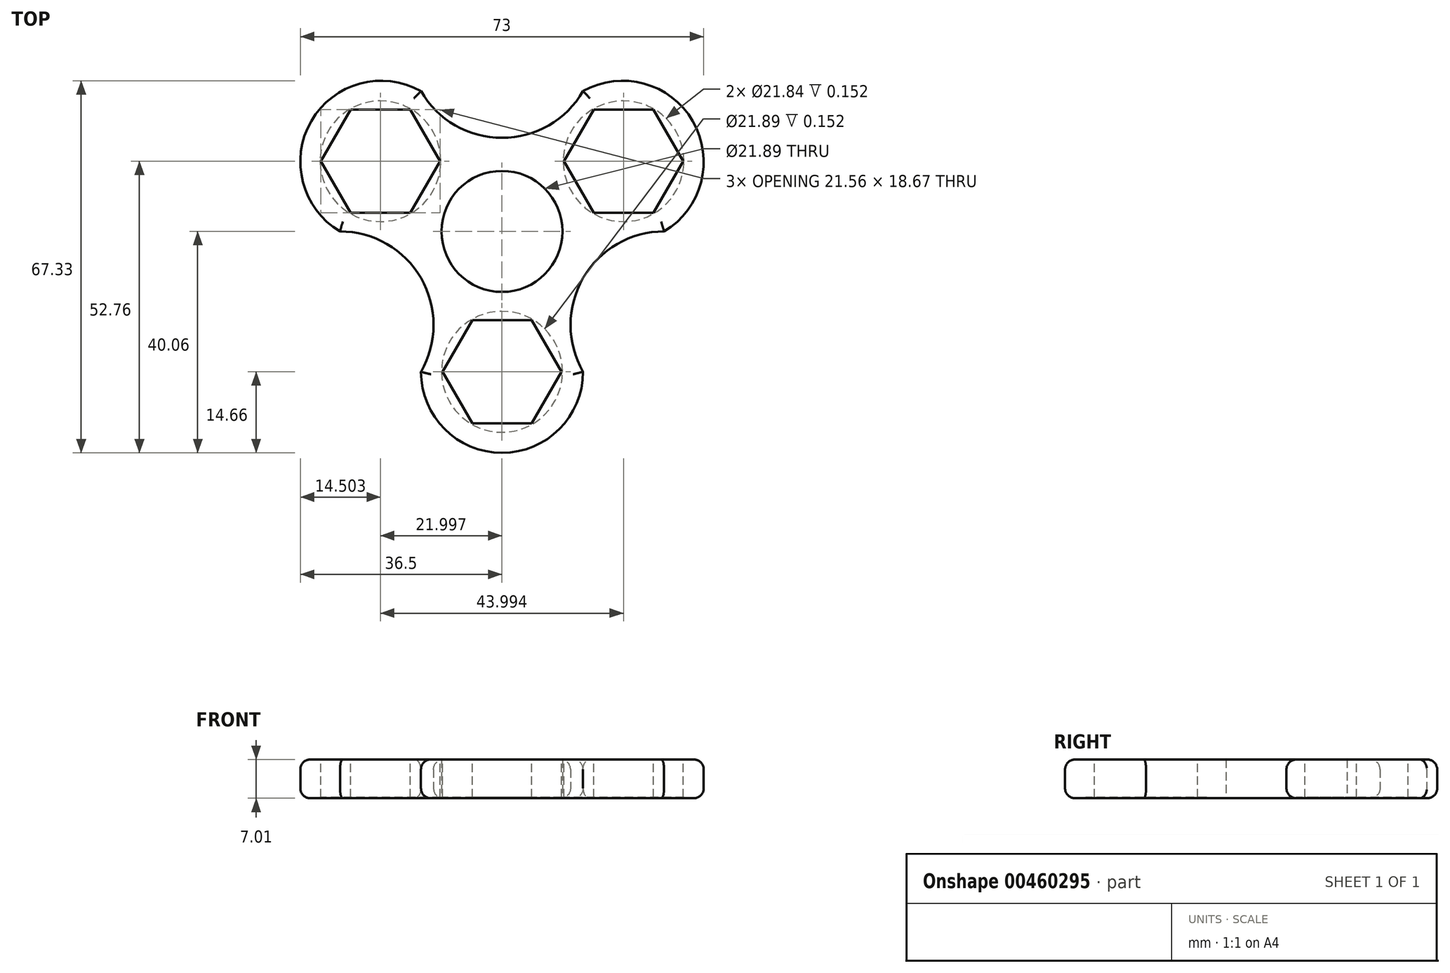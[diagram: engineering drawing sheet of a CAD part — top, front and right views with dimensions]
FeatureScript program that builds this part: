
annotation { "Feature Type Name" : "Feature", "Feature Type Description" : "" }
export const myFeature = defineFeature(function(context is Context, id is Id, definition is map)
    precondition{}
    {
        {
            var Q0;
            Q0=qCreatedBy(makeId("Top.planeOp"),FACE);
            var sketch = newSketch(context, id + "F0", { "sketchPlane" : qUnion([Q0])});
            skCircle(sketch, "E0.cCircle", {"center": v(0, 0) * mm, "radius": 12.7 * mm, "construction": true});
            skLineSegment(sketch, "E0.0", {"start": v(7.33, -12.7) * mm, "end": v(-7.33, -12.7) * mm});
            skLineSegment(sketch, "E0.1", {"start": v(-7.33, -12.7) * mm, "end": v(-14.66, 0) * mm});
            skLineSegment(sketch, "E0.2", {"start": v(-14.66, 0) * mm, "end": v(-7.33, 12.7) * mm});
            skLineSegment(sketch, "E0.4", {"start": v(7.33, 12.7) * mm, "end": v(14.66, 0) * mm});
            skLineSegment(sketch, "E0.5", {"start": v(14.66, 0) * mm, "end": v(7.33, -12.7) * mm});
            skCircle(sketch, "E1", {"center": v(0, 0) * mm, "radius": 10.95 * mm});
            skLineSegment(sketch, "E2.bottom", {"start": v(6.06, -12.7) * mm, "end": v(-4.9, -12.7) * mm});
            skLineSegment(sketch, "E3.MirrorCS", {"start": v(4.8, -76.2) * mm, "end": v(-4.8, -76.2) * mm});
            skLineSegment(sketch, "E4.MirrorCS", {"start": v(4.8, -73.66) * mm, "end": v(4.8, -76.2) * mm});
            skLineSegment(sketch, "E5.MirrorCS", {"start": v(14.66, -25.4) * mm, "end": v(7.33, -12.7) * mm});
            skCircle(sketch, "E6.MirrorC", {"center": v(0, -25.4) * mm, "radius": 12.7 * mm, "construction": true});
            skCircle(sketch, "E7.MirrorC", {"center": v(0, -25.4) * mm, "radius": 10.95 * mm});
            skLineSegment(sketch, "E8.MirrorCS", {"start": v(-7.33, -12.7) * mm, "end": v(-14.66, -25.4) * mm});
            skCircle(sketch, "E9.MirrorC", {"center": v(0, -25.4) * mm, "radius": 10.92 * mm});
            skArc(sketch, "E10", {"start": v(-14.66, -25.4) * mm, "mid": v(0, -40.06) * mm, "end": v(14.66, -25.4) * mm});
            skLineSegment(sketch, "E11", {"start": v(-7.33, 12.7) * mm, "end": v(7.33, 12.7) * mm});
            skLineSegment(sketch, "E12", {"start": v(0, 0) * mm, "end": v(0, -52.59) * mm});
            skPoint(sketch, "E12.endSnap0", {"position": v(0, -40.06) * mm});
            skLineSegment(sketch, "E13", {"start": v(0, -52.59) * mm, "end": v(0, 0) * mm});
            skLineSegment(sketch, "E14", {"start": v(0, 0) * mm, "end": v(44, 25.4) * mm});
            skLineSegment(sketch, "E15", {"start": v(44, 25.4) * mm, "end": v(0, 0) * mm});
            skLineSegment(sketch, "E16", {"start": v(0, 0) * mm, "end": v(-45.22, 26.1) * mm});
            skCircle(sketch, "E17", {"center": v(-22, 12.7) * mm, "radius": 10.92 * mm});
            skCircle(sketch, "E18", {"center": v(22, 12.7) * mm, "radius": 10.92 * mm});
            skCircle(sketch, "E19.cCircle", {"center": v(-22, 12.7) * mm, "radius": 12.7 * mm, "construction": true});
            skLineSegment(sketch, "E19.0", {"start": v(-7.33, 12.7) * mm, "end": v(-14.66, 0) * mm});
            skLineSegment(sketch, "E19.1", {"start": v(-14.66, 0) * mm, "end": v(-29.32, 0) * mm});
            skLineSegment(sketch, "E19.5", {"start": v(-14.66, 25.4) * mm, "end": v(-7.33, 12.7) * mm});
            skPoint(sketch, "E19.0.midPoint", {"position": v(-11, 6.35) * mm});
            skCircle(sketch, "E20.cCircle", {"center": v(22, 12.7) * mm, "radius": 12.7 * mm, "construction": true});
            skLineSegment(sketch, "E20.0", {"start": v(14.66, 0) * mm, "end": v(7.33, 12.7) * mm});
            skLineSegment(sketch, "E20.1", {"start": v(7.33, 12.7) * mm, "end": v(14.66, 25.4) * mm});
            skLineSegment(sketch, "E20.5", {"start": v(29.33, 0) * mm, "end": v(14.66, 0) * mm});
            skPoint(sketch, "E20.0.midPoint", {"position": v(11, 6.35) * mm});
            skArc(sketch, "E21", {"start": v(-14.66, 25.4) * mm, "mid": v(-34.54, 19.94) * mm, "end": v(-29.32, 0) * mm});
            skArc(sketch, "E22", {"start": v(29.33, 0) * mm, "mid": v(34.53, 19.94) * mm, "end": v(14.66, 25.4) * mm});
            skArc(sketch, "E23", {"start": v(-14.66, -25.4) * mm, "mid": v(-14.66, -8.47) * mm, "end": v(-29.32, 0) * mm});
            skArc(sketch, "E24", {"start": v(29.33, 0) * mm, "mid": v(14.66, -8.47) * mm, "end": v(14.66, -25.4) * mm});
            skArc(sketch, "E25", {"start": v(-14.66, 25.4) * mm, "mid": v(0, 16.93) * mm, "end": v(14.66, 25.4) * mm});
            skSolve(sketch);
        }
        {
            var Q0;
            Q0=qSketchRegion(id+"F0",true);
            var Q1;
            {var subQ8=sQuery(id+"F0.wireOp",EDGE,"E11");Q1=makeQuery(id+"F0.imprint","IMPRINT",FACE,{"disambiguationData":[TD([[makeQuery(id+"F0.imprint","IMPRINT",EDGE,{"derivedFrom":subQ8}),-1.0]])]});}
            var Q2;
            {var subQ4=sQuery(id+"F0.wireOp",EDGE,"E0.1");Q2=makeQuery(id+"F0.imprint","IMPRINT",FACE,{"disambiguationData":[TD([[makeQuery(id+"F0.imprint","IMPRINT",EDGE,{"derivedFrom":subQ4}),-1.0]])]});}
            var Q3;
            {var subQ1=sQuery(id+"F0.wireOp",EDGE,"E0.5");Q3=makeQuery(id+"F0.imprint","IMPRINT",FACE,{"disambiguationData":[TD([[makeQuery(id+"F0.imprint","IMPRINT",EDGE,{"derivedFrom":subQ1}),-1.0]])]});}
            extrude(context, id + "F1", {"entities" : qUnion([Q0, Q1, Q2, Q3]), "depth" : 7 * mm});
        }
        {
            var Q0;
            Q0=makeQuery(id+"F1.opExtrude","CAP_EDGE",EDGE,{"disambiguationData":[OSD([sQuery(id+"F0.wireOp",EDGE,"E24")])],"isStart":false});
            var Q1;
            Q1=makeQuery(id+"F1.opExtrude","CAP_EDGE",EDGE,{"disambiguationData":[OSD([sQuery(id+"F0.wireOp",EDGE,"E24")])],"isStart":true});
            var Q2;
            Q2=makeQuery(id+"F1.opExtrude","CAP_EDGE",EDGE,{"disambiguationData":[OSD([sQuery(id+"F0.wireOp",EDGE,"E10")])],"isStart":false});
            var Q3;
            Q3=makeQuery(id+"F1.opExtrude","CAP_EDGE",EDGE,{"disambiguationData":[OSD([sQuery(id+"F0.wireOp",EDGE,"E10")])],"isStart":true});
            var Q4;
            Q4=makeQuery(id+"F1.opExtrude","CAP_EDGE",EDGE,{"disambiguationData":[OSD([sQuery(id+"F0.wireOp",EDGE,"E23")])],"isStart":false});
            var Q5;
            Q5=makeQuery(id+"F1.opExtrude","CAP_EDGE",EDGE,{"disambiguationData":[OSD([sQuery(id+"F0.wireOp",EDGE,"E23")])],"isStart":true});
            var Q6;
            Q6=makeQuery(id+"F1.opExtrude","CAP_EDGE",EDGE,{"disambiguationData":[OSD([sQuery(id+"F0.wireOp",EDGE,"E21")])],"isStart":true});
            var Q7;
            Q7=makeQuery(id+"F1.opExtrude","CAP_EDGE",EDGE,{"disambiguationData":[OSD([sQuery(id+"F0.wireOp",EDGE,"E21")])],"isStart":false});
            var Q8;
            Q8=makeQuery(id+"F1.opExtrude","CAP_EDGE",EDGE,{"disambiguationData":[OSD([sQuery(id+"F0.wireOp",EDGE,"E25")])],"isStart":false});
            var Q9;
            Q9=makeQuery(id+"F1.opExtrude","CAP_EDGE",EDGE,{"disambiguationData":[OSD([sQuery(id+"F0.wireOp",EDGE,"E22")])],"isStart":false});
            var Q10;
            Q10=makeQuery(id+"F1.opExtrude","CAP_EDGE",EDGE,{"disambiguationData":[OSD([sQuery(id+"F0.wireOp",EDGE,"E22")])],"isStart":true});
            var Q11;
            Q11=makeQuery(id+"F1.opExtrude","CAP_EDGE",EDGE,{"disambiguationData":[OSD([sQuery(id+"F0.wireOp",EDGE,"E25")])],"isStart":true});
            fillet(context, id + "F2", {"entities" : qUnion([Q0, Q1, Q2, Q3, Q4, Q5, Q6, Q7, Q8, Q9, Q10, Q11]), "radius" : 1.78 * mm, "tangentPropagation" : true, "allowEdgeOverflow" : false});
        }
        {
            var Q0;
            Q0=makeQuery(id+"F1.opExtrude","CAP_FACE",FACE,{"disambiguationData":[OSD([sQuery(id+"F0.wireOp",EDGE,"E1"),sQuery(id+"F0.wireOp",EDGE,"514edc31-06ac-40e3-995b-7c1c53eea3582.MirrorCS"),sQuery(id+"F0.wireOp",EDGE,"E9.MirrorC"),sQuery(id+"F0.wireOp",EDGE,"514edc31-06ac-40e3-995b-7c1c53eea3586.MirrorCS"),sQuery(id+"F0.wireOp",EDGE,"5bda6188-825b-4b41-803b-8e19fa25ede90.MirrorCS"),sQuery(id+"F0.wireOp",EDGE,"455845eb-5c42-433d-a614-b21934a475661.MirrorCS"),sQuery(id+"F0.wireOp",EDGE,"455845eb-5c42-433d-a614-b21934a475662.MirrorCS"),sQuery(id+"F0.wireOp",EDGE,"455845eb-5c42-433d-a614-b21934a475665.MirrorC"),sQuery(id+"F0.wireOp",EDGE,"QdPQ0PJ2-Wn2Q-TIlk-QB5f-A208rq11A3H9"),sQuery(id+"F0.wireOp",EDGE,"UyywlGDB-5Jgc-yo0l-qGuh-bbdJMILhEXu3"),sQuery(id+"F0.wireOp",EDGE,"WgatU1v8-sKzI-u2eX-Sff9-52ynPzkIywBV"),sQuery(id+"F0.wireOp",EDGE,"6KD2nS0l-Hg2D-HksP-1Ouw-CZn9uDxc5PTc"),sQuery(id+"F0.wireOp",EDGE,"J5kapQ5n-iDyL-HHIj-PmFu-jLv0Z1pDbZps")])],"isStart":false});
            var sketch = newSketch(context, id + "F3", { "sketchPlane" : qUnion([Q0])});
            skCircle(sketch, "E26.cCircle", {"center": v(0, -25.4) * mm, "radius": 9.33 * mm, "construction": true});
            skLineSegment(sketch, "E26.0", {"start": v(-5.39, -16.07) * mm, "end": v(5.39, -16.07) * mm});
            skLineSegment(sketch, "E26.1", {"start": v(5.39, -16.07) * mm, "end": v(10.78, -25.4) * mm});
            skLineSegment(sketch, "E26.2", {"start": v(10.78, -25.4) * mm, "end": v(5.39, -34.73) * mm});
            skLineSegment(sketch, "E26.3", {"start": v(5.39, -34.73) * mm, "end": v(-5.39, -34.73) * mm});
            skLineSegment(sketch, "E26.4", {"start": v(-5.39, -34.73) * mm, "end": v(-10.78, -25.4) * mm});
            skLineSegment(sketch, "E26.5", {"start": v(-10.78, -25.4) * mm, "end": v(-5.39, -16.07) * mm});
            skPoint(sketch, "E26.0.midPoint", {"position": v(0, -16.07) * mm});
            skCircle(sketch, "E27", {"center": v(0, -25.4) * mm, "radius": 11.22 * mm});
            skCircle(sketch, "E28", {"center": v(22, 12.7) * mm, "radius": 10.92 * mm});
            skCircle(sketch, "E29", {"center": v(-22, 12.7) * mm, "radius": 10.92 * mm});
            skCircle(sketch, "E30.cCircle", {"center": v(-22, 12.7) * mm, "radius": 9.33 * mm, "construction": true});
            skLineSegment(sketch, "E30.0", {"start": v(-27.39, 22.03) * mm, "end": v(-16.6, 22.03) * mm});
            skLineSegment(sketch, "E30.1", {"start": v(-16.6, 22.03) * mm, "end": v(-11.22, 12.7) * mm});
            skLineSegment(sketch, "E30.2", {"start": v(-11.22, 12.7) * mm, "end": v(-16.6, 3.37) * mm});
            skLineSegment(sketch, "E30.3", {"start": v(-16.6, 3.37) * mm, "end": v(-27.39, 3.37) * mm});
            skLineSegment(sketch, "E30.4", {"start": v(-27.39, 3.37) * mm, "end": v(-32.78, 12.7) * mm});
            skLineSegment(sketch, "E30.5", {"start": v(-32.78, 12.7) * mm, "end": v(-27.39, 22.03) * mm});
            skPoint(sketch, "E30.0.midPoint", {"position": v(-22, 22.03) * mm});
            skCircle(sketch, "E31.cCircle", {"center": v(22, 12.7) * mm, "radius": 9.33 * mm, "construction": true});
            skLineSegment(sketch, "E31.0", {"start": v(16.6, 22.03) * mm, "end": v(27.39, 22.03) * mm});
            skLineSegment(sketch, "E31.1", {"start": v(27.39, 22.03) * mm, "end": v(32.78, 12.7) * mm});
            skLineSegment(sketch, "E31.2", {"start": v(32.78, 12.7) * mm, "end": v(27.39, 3.37) * mm});
            skLineSegment(sketch, "E31.3", {"start": v(27.39, 3.37) * mm, "end": v(16.6, 3.37) * mm});
            skLineSegment(sketch, "E31.4", {"start": v(16.6, 3.37) * mm, "end": v(11.22, 12.7) * mm});
            skLineSegment(sketch, "E31.5", {"start": v(11.22, 12.7) * mm, "end": v(16.6, 22.03) * mm});
            skPoint(sketch, "E31.0.midPoint", {"position": v(22, 22.03) * mm});
            skSolve(sketch);
        }
        {
            var Q0;
            Q0=makeQuery(id+"F3.imprint","IMPRINT",FACE,{"disambiguationData":[TD([[makeQuery(id+"F3.imprint","IMPRINT",EDGE,{"derivedFrom":sQuery(id+"F3.wireOp",EDGE,"E27")}),1.0]])]});
            var Q1;
            {var subQ0=sQuery(id+"F3.wireOp",EDGE,"E26.0");var subQ1=makeQuery(id+"F1.opExtrude","CAP_EDGE",EDGE,{"disambiguationData":[OSD([sQuery(id+"F0.wireOp",EDGE,"E9.MirrorC")])],"isStart":false});var subQ2=makeQuery(id+"F3.imprint","INTERSECT",VERTEX,{"disambiguationData":[OD(0.0)],"derivedFrom":[subQ1,subQ0]});Q1=makeQuery(id+"F3.imprint","IMPRINT",FACE,{"disambiguationData":[TD([[makeQuery(id+"F3.imprint","IMPRINT",EDGE,{"disambiguationData":[TD([[subQ2,-1.0]])],"derivedFrom":subQ0}),1.0]])]});}
            var Q2;
            {var subQ0=sQuery(id+"F3.wireOp",EDGE,"E26.5");var subQ1=makeQuery(id+"F1.opExtrude","CAP_EDGE",EDGE,{"disambiguationData":[OSD([sQuery(id+"F0.wireOp",EDGE,"E9.MirrorC")])],"isStart":false});var subQ2=makeQuery(id+"F3.imprint","INTERSECT",VERTEX,{"disambiguationData":[OD(0.0)],"derivedFrom":[subQ1,subQ0]});Q2=makeQuery(id+"F3.imprint","IMPRINT",FACE,{"disambiguationData":[TD([[makeQuery(id+"F3.imprint","IMPRINT",EDGE,{"disambiguationData":[TD([[subQ2,-1.0]])],"derivedFrom":subQ0}),1.0]])]});}
            var Q3;
            {var subQ0=sQuery(id+"F3.wireOp",EDGE,"E26.4");var subQ1=makeQuery(id+"F1.opExtrude","CAP_EDGE",EDGE,{"disambiguationData":[OSD([sQuery(id+"F0.wireOp",EDGE,"E9.MirrorC")])],"isStart":false});var subQ2=makeQuery(id+"F3.imprint","INTERSECT",VERTEX,{"disambiguationData":[OD(0.0)],"derivedFrom":[subQ1,subQ0]});Q3=makeQuery(id+"F3.imprint","IMPRINT",FACE,{"disambiguationData":[TD([[makeQuery(id+"F3.imprint","IMPRINT",EDGE,{"disambiguationData":[TD([[subQ2,-1.0]])],"derivedFrom":subQ0}),1.0]])]});}
            var Q4;
            {var subQ0=sQuery(id+"F3.wireOp",EDGE,"E26.3");var subQ1=makeQuery(id+"F1.opExtrude","CAP_EDGE",EDGE,{"disambiguationData":[OSD([sQuery(id+"F0.wireOp",EDGE,"E9.MirrorC")])],"isStart":false});var subQ2=makeQuery(id+"F3.imprint","INTERSECT",VERTEX,{"disambiguationData":[OD(0.0)],"derivedFrom":[subQ1,subQ0]});Q4=makeQuery(id+"F3.imprint","IMPRINT",FACE,{"disambiguationData":[TD([[makeQuery(id+"F3.imprint","IMPRINT",EDGE,{"disambiguationData":[TD([[subQ2,-1.0]])],"derivedFrom":subQ0}),1.0]])]});}
            var Q5;
            {var subQ0=sQuery(id+"F3.wireOp",EDGE,"E26.2");var subQ1=makeQuery(id+"F1.opExtrude","CAP_EDGE",EDGE,{"disambiguationData":[OSD([sQuery(id+"F0.wireOp",EDGE,"E9.MirrorC")])],"isStart":false});var subQ2=makeQuery(id+"F3.imprint","INTERSECT",VERTEX,{"disambiguationData":[OD(0.0)],"derivedFrom":[subQ1,subQ0]});Q5=makeQuery(id+"F3.imprint","IMPRINT",FACE,{"disambiguationData":[TD([[makeQuery(id+"F3.imprint","IMPRINT",EDGE,{"disambiguationData":[TD([[subQ2,-1.0]])],"derivedFrom":subQ0}),1.0]])]});}
            var Q6;
            {var subQ0=sQuery(id+"F3.wireOp",EDGE,"E26.1");var subQ1=makeQuery(id+"F1.opExtrude","CAP_EDGE",EDGE,{"disambiguationData":[OSD([sQuery(id+"F0.wireOp",EDGE,"E9.MirrorC")])],"isStart":false});var subQ2=makeQuery(id+"F3.imprint","INTERSECT",VERTEX,{"disambiguationData":[OD(0.0)],"derivedFrom":[subQ1,subQ0]});Q6=makeQuery(id+"F3.imprint","IMPRINT",FACE,{"disambiguationData":[TD([[makeQuery(id+"F3.imprint","IMPRINT",EDGE,{"disambiguationData":[TD([[subQ2,-1.0]])],"derivedFrom":subQ0}),1.0]])]});}
            var Q7;
            {var subQ0=sQuery(id+"F3.wireOp",EDGE,"E30.3");var subQ1=sQuery(id+"F3.wireOp",EDGE,"E29");var subQ2=makeQuery(id+"F3.imprint","INTERSECT",VERTEX,{"disambiguationData":[OD(0.0)],"derivedFrom":[subQ1,subQ0]});Q7=makeQuery(id+"F3.imprint","IMPRINT",FACE,{"disambiguationData":[TD([[makeQuery(id+"F3.imprint","IMPRINT",EDGE,{"disambiguationData":[TD([[subQ2,-1.0]])],"derivedFrom":subQ1}),1.0]])]});}
            var Q8;
            {var subQ0=sQuery(id+"F3.wireOp",EDGE,"E30.5");var subQ1=sQuery(id+"F3.wireOp",EDGE,"E29");var subQ2=makeQuery(id+"F3.imprint","INTERSECT",VERTEX,{"disambiguationData":[OD(0.0)],"derivedFrom":[subQ1,subQ0]});Q8=makeQuery(id+"F3.imprint","IMPRINT",FACE,{"disambiguationData":[TD([[makeQuery(id+"F3.imprint","IMPRINT",EDGE,{"disambiguationData":[TD([[subQ2,-1.0]])],"derivedFrom":subQ1}),1.0]])]});}
            var Q9;
            {var subQ0=sQuery(id+"F3.wireOp",EDGE,"E30.0");var subQ1=sQuery(id+"F3.wireOp",EDGE,"E29");var subQ2=makeQuery(id+"F3.imprint","INTERSECT",VERTEX,{"disambiguationData":[OD(0.0)],"derivedFrom":[subQ1,subQ0]});Q9=makeQuery(id+"F3.imprint","IMPRINT",FACE,{"disambiguationData":[TD([[makeQuery(id+"F3.imprint","IMPRINT",EDGE,{"disambiguationData":[TD([[subQ2,-1.0]])],"derivedFrom":subQ1}),1.0]])]});}
            var Q10;
            {var subQ0=sQuery(id+"F3.wireOp",EDGE,"E30.4");var subQ1=sQuery(id+"F3.wireOp",EDGE,"E29");var subQ2=makeQuery(id+"F3.imprint","INTERSECT",VERTEX,{"disambiguationData":[OD(0.0)],"derivedFrom":[subQ1,subQ0]});Q10=makeQuery(id+"F3.imprint","IMPRINT",FACE,{"disambiguationData":[TD([[makeQuery(id+"F3.imprint","IMPRINT",EDGE,{"disambiguationData":[TD([[subQ2,-1.0]])],"derivedFrom":subQ1}),1.0]])]});}
            var Q11;
            {var subQ0=sQuery(id+"F3.wireOp",EDGE,"E30.1");var subQ1=sQuery(id+"F3.wireOp",EDGE,"E29");var subQ2=makeQuery(id+"F3.imprint","INTERSECT",VERTEX,{"disambiguationData":[OD(0.0)],"derivedFrom":[subQ1,subQ0]});Q11=makeQuery(id+"F3.imprint","IMPRINT",FACE,{"disambiguationData":[TD([[makeQuery(id+"F3.imprint","IMPRINT",EDGE,{"disambiguationData":[TD([[subQ2,1.0]])],"derivedFrom":subQ1}),1.0]])]});}
            var Q12;
            {var subQ0=sQuery(id+"F3.wireOp",EDGE,"E30.2");var subQ1=sQuery(id+"F3.wireOp",EDGE,"E29");var subQ2=makeQuery(id+"F3.imprint","INTERSECT",VERTEX,{"disambiguationData":[OD(0.0)],"derivedFrom":[subQ1,subQ0]});Q12=makeQuery(id+"F3.imprint","IMPRINT",FACE,{"disambiguationData":[TD([[makeQuery(id+"F3.imprint","IMPRINT",EDGE,{"disambiguationData":[TD([[subQ2,-1.0]])],"derivedFrom":subQ1}),1.0]])]});}
            var Q13;
            {var subQ0=sQuery(id+"F3.wireOp",EDGE,"E31.4");var subQ1=sQuery(id+"F3.wireOp",EDGE,"E28");var subQ2=makeQuery(id+"F3.imprint","INTERSECT",VERTEX,{"disambiguationData":[OD(0.0)],"derivedFrom":[subQ1,subQ0]});Q13=makeQuery(id+"F3.imprint","IMPRINT",FACE,{"disambiguationData":[TD([[makeQuery(id+"F3.imprint","IMPRINT",EDGE,{"disambiguationData":[TD([[subQ2,-1.0]])],"derivedFrom":subQ1}),1.0]])]});}
            var Q14;
            {var subQ0=sQuery(id+"F3.wireOp",EDGE,"E31.5");var subQ1=sQuery(id+"F3.wireOp",EDGE,"E28");var subQ2=makeQuery(id+"F3.imprint","INTERSECT",VERTEX,{"disambiguationData":[OD(0.0)],"derivedFrom":[subQ1,subQ0]});Q14=makeQuery(id+"F3.imprint","IMPRINT",FACE,{"disambiguationData":[TD([[makeQuery(id+"F3.imprint","IMPRINT",EDGE,{"disambiguationData":[TD([[subQ2,-1.0]])],"derivedFrom":subQ1}),1.0]])]});}
            var Q15;
            {var subQ0=sQuery(id+"F3.wireOp",EDGE,"E31.0");var subQ1=sQuery(id+"F3.wireOp",EDGE,"E28");var subQ2=makeQuery(id+"F3.imprint","INTERSECT",VERTEX,{"disambiguationData":[OD(0.0)],"derivedFrom":[subQ1,subQ0]});Q15=makeQuery(id+"F3.imprint","IMPRINT",FACE,{"disambiguationData":[TD([[makeQuery(id+"F3.imprint","IMPRINT",EDGE,{"disambiguationData":[TD([[subQ2,-1.0]])],"derivedFrom":subQ1}),1.0]])]});}
            var Q16;
            {var subQ0=sQuery(id+"F3.wireOp",EDGE,"E31.1");var subQ1=sQuery(id+"F3.wireOp",EDGE,"E28");var subQ2=makeQuery(id+"F3.imprint","INTERSECT",VERTEX,{"disambiguationData":[OD(0.0)],"derivedFrom":[subQ1,subQ0]});Q16=makeQuery(id+"F3.imprint","IMPRINT",FACE,{"disambiguationData":[TD([[makeQuery(id+"F3.imprint","IMPRINT",EDGE,{"disambiguationData":[TD([[subQ2,1.0]])],"derivedFrom":subQ1}),1.0]])]});}
            var Q17;
            {var subQ0=sQuery(id+"F3.wireOp",EDGE,"E31.2");var subQ1=sQuery(id+"F3.wireOp",EDGE,"E28");var subQ2=makeQuery(id+"F3.imprint","INTERSECT",VERTEX,{"disambiguationData":[OD(0.0)],"derivedFrom":[subQ1,subQ0]});Q17=makeQuery(id+"F3.imprint","IMPRINT",FACE,{"disambiguationData":[TD([[makeQuery(id+"F3.imprint","IMPRINT",EDGE,{"disambiguationData":[TD([[subQ2,-1.0]])],"derivedFrom":subQ1}),1.0]])]});}
            var Q18;
            {var subQ0=sQuery(id+"F3.wireOp",EDGE,"E31.3");var subQ1=sQuery(id+"F3.wireOp",EDGE,"E28");var subQ2=makeQuery(id+"F3.imprint","INTERSECT",VERTEX,{"disambiguationData":[OD(0.0)],"derivedFrom":[subQ1,subQ0]});Q18=makeQuery(id+"F3.imprint","IMPRINT",FACE,{"disambiguationData":[TD([[makeQuery(id+"F3.imprint","IMPRINT",EDGE,{"disambiguationData":[TD([[subQ2,-1.0]])],"derivedFrom":subQ1}),1.0]])]});}
            extrude(context, id + "F4", {"entities" : qUnion([Q0, Q1, Q2, Q3, Q4, Q5, Q6, Q7, Q8, Q9, Q10, Q11, Q12, Q13, Q14, Q15, Q16, Q17, Q18]), "operationType" : NewBodyOperationType.ADD, "depth" : -6.86 * mm});
        }
    });
